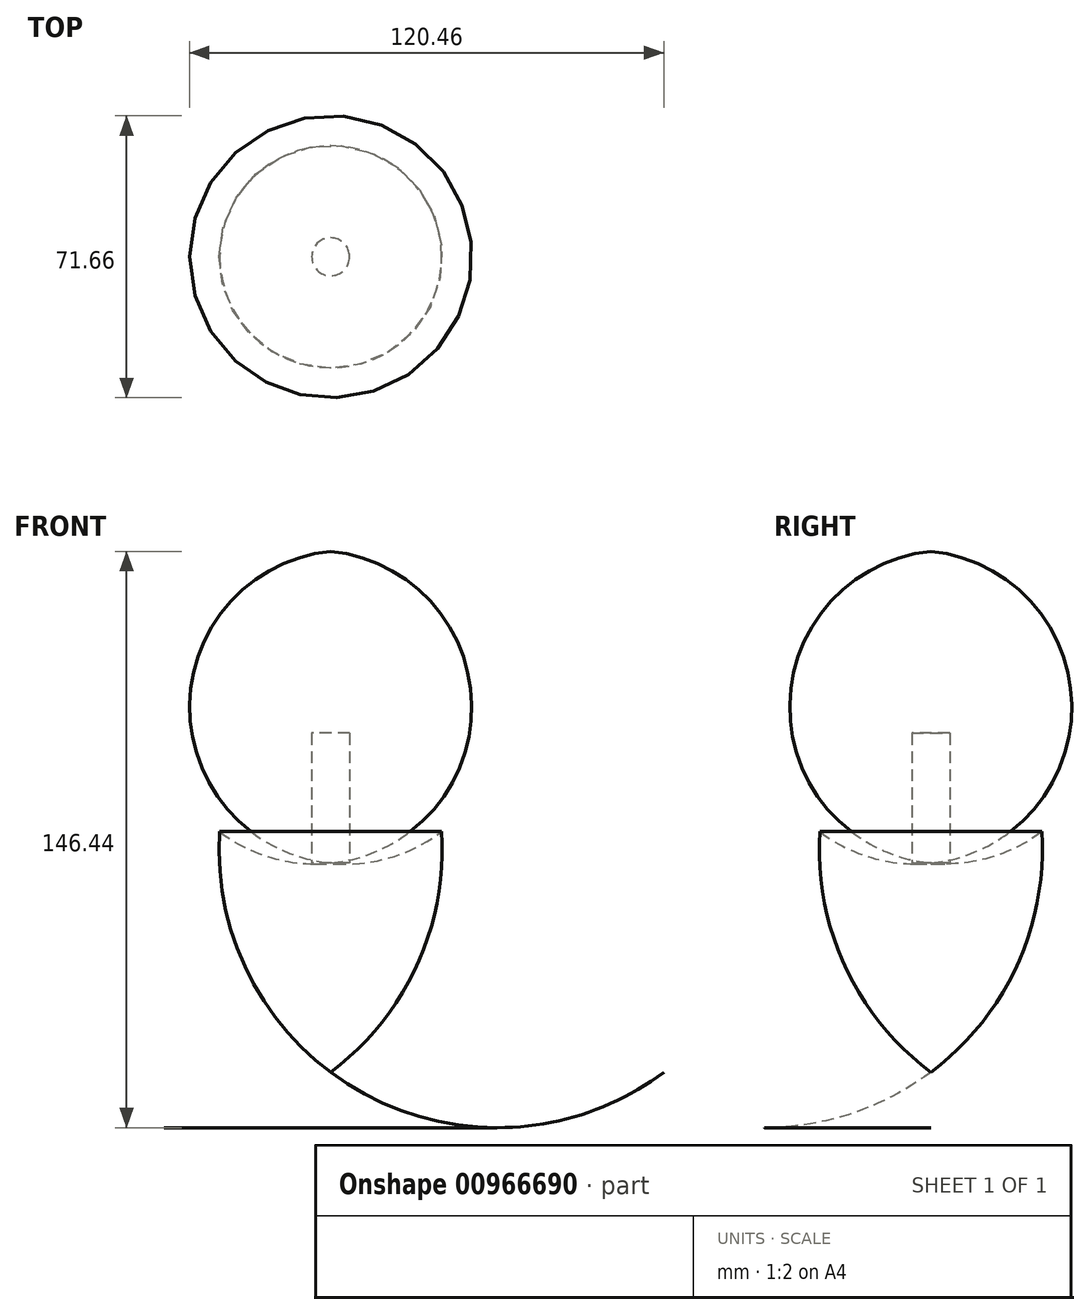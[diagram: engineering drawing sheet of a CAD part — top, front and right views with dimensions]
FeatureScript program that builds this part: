
annotation { "Feature Type Name" : "Feature", "Feature Type Description" : "" }
export const myFeature = defineFeature(function(context is Context, id is Id, definition is map)
    precondition{}
    {
        {
            var Q0;
            Q0=qCreatedBy(makeId("Front.planeOp"),FACE);
            var sketch = newSketch(context, id + "F0", { "sketchPlane" : qUnion([Q0])});
            skArc(sketch, "E0", {"start": v(0, 0) * mm, "mid": v(14.85, 1.31) * mm, "end": v(28.18, 8) * mm});
            skArc(sketch, "E1", {"start": v(0, -53.14) * mm, "mid": v(21.84, -26.14) * mm, "end": v(28.18, 8) * mm});
            skLineSegment(sketch, "E2", {"start": v(0, 0) * mm, "end": v(0, -53.14) * mm});
            skSolve(sketch);
        }
        {
            var Q0;
            Q0=makeQuery(id+"F0.imprint","IMPRINT",FACE,{"disambiguationData":[TD([[makeQuery(id+"F0.imprint","IMPRINT",EDGE,{"derivedFrom":sQuery(id+"F0.wireOp",EDGE,"E0")}),-1.0]])]});
            var Q1;
            Q1=sQuery(id+"F0.wireOp",EDGE,"E2");
            revolve(context, id + "F1", {"surfaceOperationType" : NewSurfaceOperationType.NEW, "entities" : qUnion([Q0]), "axis" : qUnion([Q1]), "revolveType" : RevolveType.FULL});
        }
        {
            var Q0;
            Q0=qCreatedBy(makeId("Top.planeOp"),FACE);
            var sketch = newSketch(context, id + "F2", { "sketchPlane" : qUnion([Q0])});
            skCircle(sketch, "E3", {"center": v(0, 0) * mm, "radius": 4.81 * mm});
            skSolve(sketch);
        }
        {
            var Q0;
            Q0=makeQuery(id+"F2.imprint","IMPRINT",FACE,{"disambiguationData":[TD([[makeQuery(id+"F2.imprint","IMPRINT",EDGE,{"derivedFrom":sQuery(id+"F2.wireOp",EDGE,"E3")}),1.0]])]});
            extrude(context, id + "F3", {"entities" : qUnion([Q0]), "depth" : 33.02 * mm, "offsetDistance" : 25.4 * mm});
        }
    });
